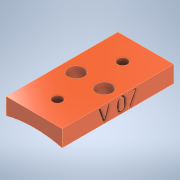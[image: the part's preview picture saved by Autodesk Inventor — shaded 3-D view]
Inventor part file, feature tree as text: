
AUTODESK INVENTOR PART (.ipt)
format: ipt  version: 2021 (Build 250183000, 183)  size: 254,976 bytes
history: native  units: in
note: dims shown in document units (in); Inventor stores cm internally (conversion verified against a paired STEP export)
features: sketch x4, extrude x3, hole x1
ambient origin geometry x8: Origin, YZ Plane, XZ Plane, XY Plane, X Axis, Y Axis, Z Axis, Center Point
bodies: Solid1 (feature_tree)
feature tree (8):
  extrude  "Extrusion1"  Depth=0.75in
  hole  "Hole2"  [1 undecoded]
  extrude  "Extrusion8"  TaperAngle=60.0deg  [1 undecoded]
  extrude  "Extrusion9"  TaperAngle=60.0deg  [1 undecoded]
  sketch  "Sketch1"  dims[d0=6.0in d1=0.75in]
  sketch  "Sketch23"  dims[d2=0.45in d3=3.0in d4=0.0in]
  sketch  "Sketch24"  dims[d51=0.0039in d53=60.0deg]
  sketch  "Sketch25"  dims[d72=0.0039in d74=60.0deg d93=0.0039in d95=60.0deg d114=0.0039in d116=60.0deg d135=0.0039in d137=60.0deg d156=0.0039in d158=60.0deg d183=0.625in d184=0.625in d185=0.201in d186=0.38in d187=0.257in d188=0.31in d189=0.5635in d190=1.0in d191=0.8108in d192=0.375in d194=0.375in d195=0.75in d196=0.0in d197=0.0in d199=0.425in d200=0.425in d201=0.1in d202=0.0in]
note: 3 required parameter values undecoded (feature->parameter linkage not recoverable at this tier; creation-order binding heuristic only, values carry confidence <= 0.55)
